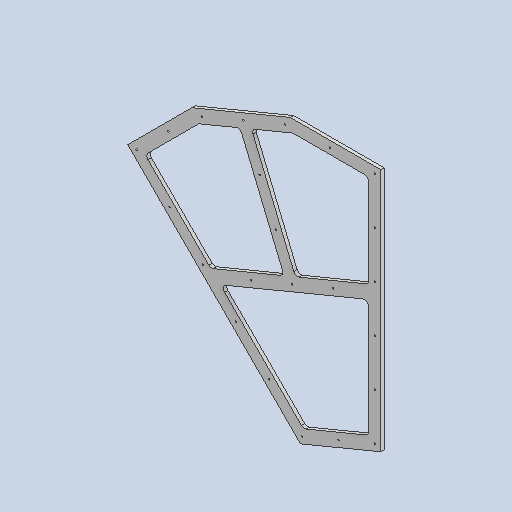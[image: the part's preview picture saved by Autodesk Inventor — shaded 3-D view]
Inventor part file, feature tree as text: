
AUTODESK INVENTOR PART (.ipt)
format: ipt  version: 2025 (Build 290162010, 162A)  size: 176,640 bytes
history: native  units: mm
features: other x3, sketch x2
ambient origin geometry x8: Origin, YZ Plane, XZ Plane, XY Plane, X Axis, Y Axis, Z Axis, Center Point
bodies: Solid1 (feature_tree)
feature tree (5):
  other  "ДМС 206 Крепление сетки к кассете"
  other  "Solid1::ДМС 206 Крепление сетки к кассете"
  other  "TaggingFeature1"
  sketch  "Sketch1"  dims[d0=10.0mm]
  sketch  "Sketch2"
